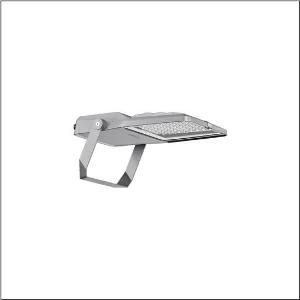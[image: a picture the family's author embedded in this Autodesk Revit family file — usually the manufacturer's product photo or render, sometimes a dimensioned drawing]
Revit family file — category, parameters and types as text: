
# Revit family: floodlight_fl_21_iq_mini___rs12_5xa7772b1b1a_07b1
name_source: partatom
category: Lighting Fixtures
units: mm (PartAtom-declared; Revit-internal decimal feet)

## family parameters
Cut with Voids When Loaded = No
Host = Face
Light Source = No
Part Type = Normal
Room Calculation Point = No
Round Connector Dimension = Use Diameter
Shared = No

## types (1)
- --- (1 x LED, 5230 lm, 45.5 W, 2200K)
    Apparent Load = 46 VA
    CIE Flux Codes = 79 92 99 100 100
    Color Rendering = 70
    Color Temperature = 2200K
    Default Elevation = 1800 mm
    Description = Floodlight FL 21 iQ mini, floodlight, primary light control with lens, of PMMA, primary optical cover: protective disc, of toughened safety glass, transparent, light distribution: RS12, light emission: direct distribution, installation type: surface-mounted, LED, High Power LED, rated luminous flux: 5.230lm, luminous efficacy: 115lm/W, light colour: 722, colour temperature: 2200K, control: Street-Remote, Auto-Match, Temp-Guard, Night-Set, Smart-Wire, Desk-Remote (wireless, voltage-free reading and setting of iQ features in the workshop via application-optimized NFC function/RFID function), optimised constant luminous flux control (CLO 2.0), with terminal, 6-pole, mains connection: 220..240V, AC, 50/60Hz, start of lifetime: 46W, end of service life: 48W, reduction: 21W, luminaire housing, of diecast aluminium, powder-coated, Siteco® metallic grey (DB 702S), corrosivity category C5 mid according to DIN EN ISO 12944, sealing non-destructively replaceable, mounting bracket, of steel, galvanised, powder-coated, Siteco® metallic grey (DB 702S), protection rating (complete): IP66, insulation class (complete): insulation class II (safety insulation), certification: CE, ENEC, VDE, protection symbol: D, impact resistance: IK08, permissible operating ambient temperature: -40..+40°C, permissible operating ambient temperature for outdoor applications: -40..+50°C, standard: DIN EN 12944, LABS conformity tested according to VDMA 24364:2018-05, packaging unit: 1 piece

Light Distribution: RS12
    Height = 70 mm
    Lamp = 1 x LED
    Lamp Light Flux = 5230 lm
    Lamp Power = 45.5 W
    Lamp count = 1
    Length = 485 mm
    Luminous efficacy = 115 lm/W
    Manufacturer = Siteco
    ModVariant = No
    Model = 5XA7772B1B1A
    Number of Poles = 1
    OnlyDefault = Yes
    Power Factor = 1
    Product Name = Floodlight FL 21 iQ mini | RS12
    Product group = floodlight | pylon annexe
    ProductGroupID = 6200
    Protection Class = Protection class II
    Protection Degree = IP 66
    RLX_Detail_Level = 1
    RLX_Emergency_Light_Flux = 0 lm
    RLX_Emergency_Type = 0
    RLX_Emergency_Type_DB = No
    RlxData = <blob elided: 90809 chars, md5=ddf63373>
    Socket = socket
    Standby Power = 0 W
    System Light Flux = 5230 lm
    System Power = 46 W
    Type Comments = factory setting: luminous flux: 100 % | dim-lin: 254 | 463 mA
    Type Image = l_1006845.jpg
    URL = http://relux.com
    VarID = @adj_100239
    Voltage = 0 V
    Weight = 0.00 kg
    Width = 337 mm

## geometry (parser evidence)
native form markers: Blend x4, Sweep x15
no freeform markers — native parametric forms only
